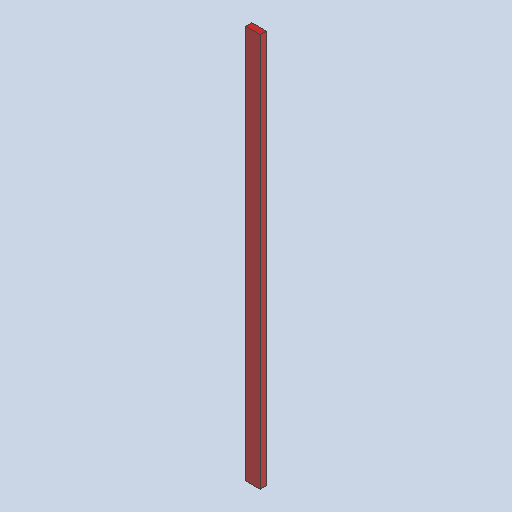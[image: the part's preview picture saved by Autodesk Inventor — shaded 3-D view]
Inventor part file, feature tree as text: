
AUTODESK INVENTOR PART (.ipt)
format: ipt  version: 2025 (Build 290162000, 162)  size: 82,944 bytes
history: native  units: in
note: dims shown in document units (in); Inventor stores cm internally (conversion verified against a paired STEP export)
features: extrude x1, sketch x1, other x1
ambient origin geometry x8: Origin, YZ Plane, XZ Plane, XY Plane, X Axis, Y Axis, Z Axis, Center Point
bodies: Solid1 (feature_tree)
feature tree (3):
  extrude  "Extrusion1"  Depth=3.5in
  sketch  "Sketch1"  dims[d0=1.5in d1=3.5in d2=96.0in d3=0.0in]
  other  "Finish1"
